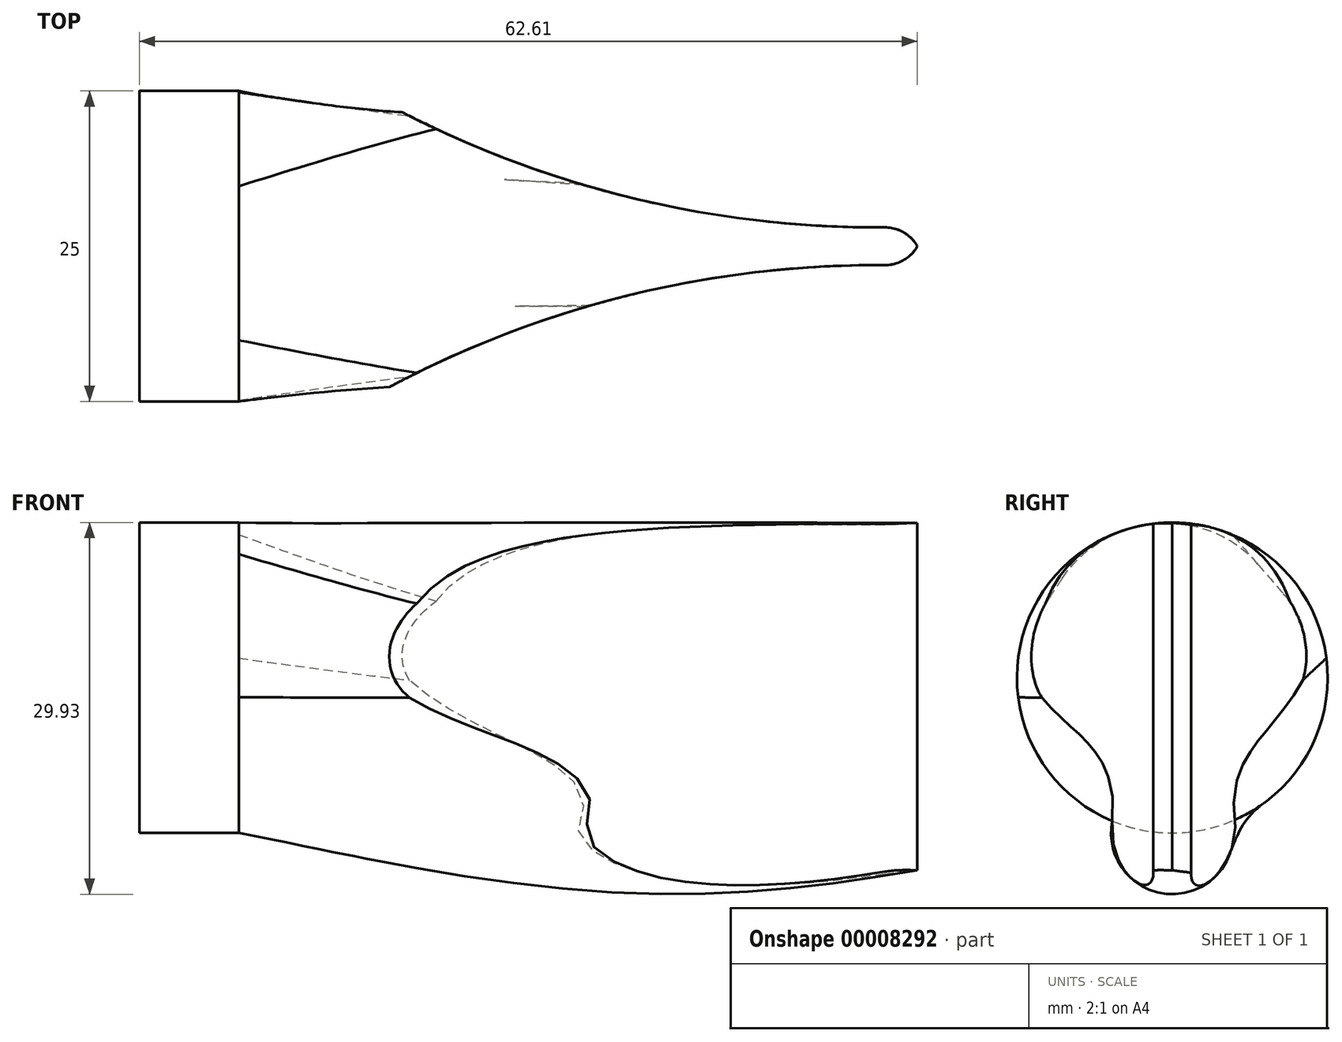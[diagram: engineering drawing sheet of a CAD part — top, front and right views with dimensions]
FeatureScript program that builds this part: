
annotation { "Feature Type Name" : "Feature", "Feature Type Description" : "" }
export const myFeature = defineFeature(function(context is Context, id is Id, definition is map)
    precondition{}
    {
        {
            var Q0;
            Q0=qCreatedBy(makeId("Right.planeOp"),FACE);
            var sketch = newSketch(context, id + "F0", { "sketchPlane" : qUnion([Q0])});
            skCircle(sketch, "E0", {"center": v(0, 0) * mm, "radius": 12.5 * mm});
            skLineSegment(sketch, "E1", {"start": v(0, 0) * mm, "end": v(0, 12.5) * mm});
            skSolve(sketch);
        }
        {
            var Q0;
            Q0=qCreatedBy(makeId("Right.planeOp"),FACE);
            cPlane(context, id + "F1", {"entities" : qUnion([Q0]), "cplaneType" : CPlaneType.OFFSET, "offset" : 35 * mm, "width" : 150 * mm, "height" : 150 * mm});
        }
        {
            var Q0;
            Q0=qCreatedBy(id+"F1.planeOp",FACE);
            var sketch = newSketch(context, id + "F2", { "sketchPlane" : qUnion([Q0])});
            skArc(sketch, "E2", {"start": v(-4.83, -11.53) * mm, "mid": v(0, -17.43) * mm, "end": v(4.83, -11.53) * mm});
            skArc(sketch, "E3", {"start": v(-4.83, -11.53) * mm, "mid": v(-5.5, -5.97) * mm, "end": v(-9, -1.6) * mm});
            skLineSegment(sketch, "E4", {"start": v(0, 0) * mm, "end": v(0, 12.5) * mm});
            skArc(sketch, "E5.0.MirrorCS", {"start": v(4.83, -11.53) * mm, "mid": v(5.5, -5.97) * mm, "end": v(9, -1.6) * mm});
            skArc(sketch, "E6", {"start": v(-12.11, 3.1) * mm, "mid": v(-11.05, 0.41) * mm, "end": v(-9, -1.6) * mm});
            skArc(sketch, "E7.0.MirrorCS", {"start": v(12.11, 3.1) * mm, "mid": v(11.05, 0.41) * mm, "end": v(9, -1.6) * mm});
            skPoint(sketch, "E8.trimOffspring.end.orphan", {"position": v(12.5, 0) * mm});
            skArc(sketch, "E9.trimOffspring", {"start": v(12.11, 3.1) * mm, "mid": v(0, 12.5) * mm, "end": v(-12.11, 3.1) * mm});
            skPoint(sketch, "E10.start.orphan", {"position": v(-12.5, 0) * mm});
            skSolve(sketch);
        }
        {
            var Q0;
            Q0=qCreatedBy(id+"F1.planeOp",FACE);
            cPlane(context, id + "F3", {"entities" : qUnion([Q0]), "cplaneType" : CPlaneType.OFFSET, "offset" : 35 * mm, "width" : 150 * mm, "height" : 150 * mm});
        }
        {
            var Q0;
            Q0=qCreatedBy(id+"F3.planeOp",FACE);
            var sketch = newSketch(context, id + "F4", { "sketchPlane" : qUnion([Q0])});
            skCircle(sketch, "E11", {"center": v(0, 0) * mm, "radius": 12.5 * mm});
            skSolve(sketch);
        }
        {
            var Q0;
            Q0=makeQuery(id+"F0.imprint","IMPRINT",FACE,{"disambiguationData":[TD([[makeQuery(id+"F0.imprint","IMPRINT",EDGE,{"derivedFrom":sQuery(id+"F0.wireOp",EDGE,"E0")}),1.0]])]});
            var Q1;
            Q1=makeQuery(id+"F2.imprint","IMPRINT",FACE,{"disambiguationData":[TD([[makeQuery(id+"F2.imprint","IMPRINT",EDGE,{"derivedFrom":sQuery(id+"F2.wireOp",EDGE,"E2")}),1.0]])]});
            var Q2;
            Q2=makeQuery(id+"F4.imprint","IMPRINT",FACE,{"disambiguationData":[TD([[makeQuery(id+"F4.imprint","IMPRINT",EDGE,{"derivedFrom":sQuery(id+"F4.wireOp",EDGE,"E11")}),1.0]])]});
            loft(context, id + "F5", {"sheetProfilesArray" : [{ "sheetProfileEntities" : qUnion([Q0]) }, { "sheetProfileEntities" : qUnion([Q1]) }, { "sheetProfileEntities" : qUnion([Q2]) }]});
        }
        {
            var Q0;
            Q0=makeQuery(id+"F5.opLoft","CAP_FACE",FACE,{"disambiguationData":[OSD([makeQuery(id+"F4.imprint","IMPRINT",FACE,{"disambiguationData":[TD([[makeQuery(id+"F4.imprint","IMPRINT",EDGE,{"derivedFrom":sQuery(id+"F4.wireOp",EDGE,"E11")}),1.0]])]})])],"isStart":true});
            extrude(context, id + "F6", {"entities" : qUnion([Q0]), "operationType" : NewBodyOperationType.ADD, "depth" : 5 * mm});
        }
        {
            var Q0;
            Q0=makeQuery(id+"F5.opLoft","CAP_FACE",FACE,{"disambiguationData":[OSD([makeQuery(id+"F0.imprint","IMPRINT",FACE,{"disambiguationData":[TD([[makeQuery(id+"F0.imprint","IMPRINT",EDGE,{"derivedFrom":sQuery(id+"F0.wireOp",EDGE,"E0")}),1.0]])]})])],"isStart":true});
            extrude(context, id + "F7", {"entities" : qUnion([Q0]), "operationType" : NewBodyOperationType.ADD, "depth" : 8 * mm});
        }
        {
            var Q0;
            Q0=qCreatedBy(makeId("Top.planeOp"),FACE);
            var sketch = newSketch(context, id + "F8", { "sketchPlane" : qUnion([Q0])});
            skLineSegment(sketch, "E12", {"start": v(0, 0) * mm, "end": v(0, 25.02) * mm});
            skLineSegment(sketch, "E13", {"start": v(0, 0) * mm, "end": v(55, 0) * mm});
            skArc(sketch, "E14", {"start": v(10, 12.5) * mm, "mid": v(31.73, 3.87) * mm, "end": v(55, 1.6) * mm});
            skLineSegment(sketch, "E15", {"start": v(10, 12.5) * mm, "end": v(55, 13.67) * mm});
            skPoint(sketch, "E16.orphan", {"position": v(10, 25.02) * mm});
            skArc(sketch, "E17.0.MirrorCS", {"start": v(10, -12.5) * mm, "mid": v(31.73, -3.87) * mm, "end": v(55, -1.6) * mm});
            skLineSegment(sketch, "E18.0.MirrorCS", {"start": v(10, -12.5) * mm, "end": v(55, -13.67) * mm});
            skLineSegment(sketch, "E19", {"start": v(55, 1.6) * mm, "end": v(55, -1.6) * mm});
            skLineSegment(sketch, "E20", {"start": v(55, 13.67) * mm, "end": v(83.75, 13.67) * mm});
            skLineSegment(sketch, "E21", {"start": v(55, -13.67) * mm, "end": v(83.75, -13.67) * mm});
            skLineSegment(sketch, "E22", {"start": v(83.75, -13.67) * mm, "end": v(83.75, 13.67) * mm});
            skPoint(sketch, "E23.0.start.orphan", {"position": v(10, 0) * mm});
            skSolve(sketch);
        }
        {
            var Q0;
            Q0 = qSketchRegion(id + "F8", true);
            extrude(context, id + "F9", {"entities" : qUnion([Q0]), "operationType" : NewBodyOperationType.REMOVE, "endBound" : BoundingType.SYMMETRIC, "oppositeDirection" : true, "depth" : 45 * mm});
        }
        {
            var Q0;
            {var subQ0=sQuery(id+"F2.wireOp",EDGE,"E9.trimOffspring");var subQ1=sQuery(id+"F2.wireOp",EDGE,"E7.0.MirrorCS");var subQ2=sQuery(id+"F2.wireOp",EDGE,"E5.0.MirrorCS");var subQ3=sQuery(id+"F0.wireOp",EDGE,"E0");var subQ4=sQuery(id+"F8.wireOp",EDGE,"E17.0.MirrorCS");var subQ5=sQuery(id+"F8.wireOp",EDGE,"E19");Q0=makeQuery(id+"F9.boolean.opBoolean","COPY",EDGE,{"disambiguationData":[TD([makeQuery(id+"F5.opLoft","SWEPT_FACE",FACE,{"disambiguationData":[OSD([subQ3,subQ2,subQ1,subQ0])]})])],"derivedFrom":makeQuery(id+"F9.opExtrude","SWEPT_EDGE",EDGE,{"disambiguationData":[OSD([subQ4,subQ5])]})});}
            var Q1;
            {var subQ0=sQuery(id+"F2.wireOp",EDGE,"E9.trimOffspring");var subQ1=sQuery(id+"F2.wireOp",EDGE,"E7.0.MirrorCS");var subQ2=sQuery(id+"F2.wireOp",EDGE,"E5.0.MirrorCS");var subQ3=sQuery(id+"F0.wireOp",EDGE,"E0");var subQ4=sQuery(id+"F8.wireOp",EDGE,"E14");var subQ5=sQuery(id+"F8.wireOp",EDGE,"E19");Q1=makeQuery(id+"F9.boolean.opBoolean","COPY",EDGE,{"disambiguationData":[TD([makeQuery(id+"F5.opLoft","SWEPT_FACE",FACE,{"disambiguationData":[OSD([subQ3,subQ2,subQ1,subQ0])]})])],"derivedFrom":makeQuery(id+"F9.opExtrude","SWEPT_EDGE",EDGE,{"disambiguationData":[OSD([subQ4,subQ5])]})});}
            fillet(context, id + "F10", {"entities" : qUnion([Q0, Q1]), "radius" : 3 * mm, "tangentPropagation" : true, "allowEdgeOverflow" : false});
        }
    });
